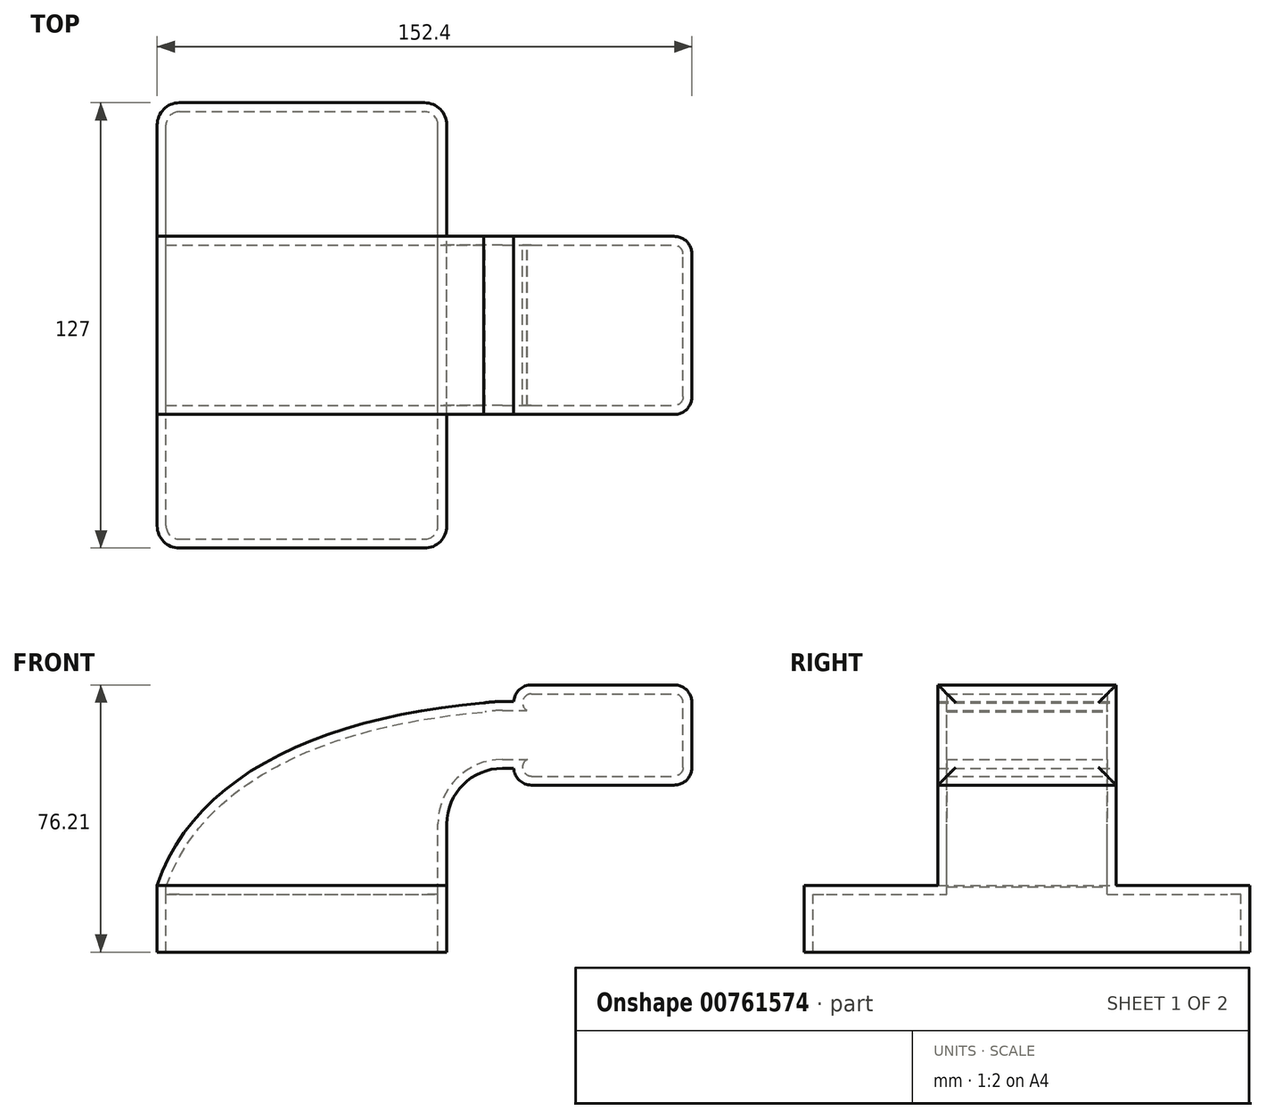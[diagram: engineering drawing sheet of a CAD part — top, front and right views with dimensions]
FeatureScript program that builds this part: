
annotation { "Feature Type Name" : "Feature", "Feature Type Description" : "" }
export const myFeature = defineFeature(function(context is Context, id is Id, definition is map)
    precondition{}
    {
        {
            var Q0;
            Q0=qCreatedBy(makeId("Front.planeOp"),FACE);
            var sketch = newSketch(context, id + "F0", { "sketchPlane" : qUnion([Q0])});
            skLineSegment(sketch, "E0.bottom", {"start": v(-41.28, -9.53) * mm, "end": v(41.28, -9.53) * mm});
            skLineSegment(sketch, "E0.top", {"start": v(-41.28, 9.52) * mm, "end": v(41.28, 9.52) * mm});
            skLineSegment(sketch, "E0.left", {"start": v(-41.28, -9.53) * mm, "end": v(-41.28, 9.53) * mm});
            skLineSegment(sketch, "E0.right", {"start": v(41.28, -9.53) * mm, "end": v(41.28, 9.52) * mm});
            skPoint(sketch, "E0.middle", {"position": v(0, 0) * mm});
            skLineSegment(sketch, "E1.bottom", {"start": v(60.33, 38.1) * mm, "end": v(111.13, 38.1) * mm});
            skLineSegment(sketch, "E1.top", {"start": v(60.33, 66.67) * mm, "end": v(111.13, 66.67) * mm});
            skLineSegment(sketch, "E1.left", {"start": v(60.33, 38.1) * mm, "end": v(60.33, 66.67) * mm});
            skLineSegment(sketch, "E1.right", {"start": v(111.13, 38.1) * mm, "end": v(111.13, 66.67) * mm});
            skPoint(sketch, "E1.middle", {"position": v(85.73, 52.39) * mm});
            skLineSegment(sketch, "E2", {"start": v(41.27, 9.52) * mm, "end": v(41.27, 27) * mm});
            skArc(sketch, "E3", {"start": v(41.27, 27) * mm, "mid": v(45.92, 38.23) * mm, "end": v(57.15, 42.88) * mm});
            skLineSegment(sketch, "E4", {"start": v(57.15, 42.88) * mm, "end": v(85.82, 42.88) * mm});
            skLineSegment(sketch, "E5.0", {"start": v(57.15, 61.93) * mm, "end": v(85.82, 61.93) * mm});
            skArc(sketch, "E5.1", {"start": v(22.23, 27) * mm, "mid": v(32.45, 51.7) * mm, "end": v(57.15, 61.93) * mm});
            skLineSegment(sketch, "E5.2", {"start": v(22.22, 9.52) * mm, "end": v(22.22, 27) * mm});
            skLineSegment(sketch, "E6", {"start": v(85.82, 38.1) * mm, "end": v(85.82, 66.67) * mm});
            skFitSpline(sketch, "E7", {"points": [v(-41.28, 9.53) * mm, v(57.15, 61.93) * mm], "startDerivative": vector(32.2, 96.48) * mm, "endDerivative": vector(149.38, 9.9) * mm});
            skSolve(sketch);
        }
        {
            var Q0;
            Q0=makeQuery(id+"F0.imprint","IMPRINT",FACE,{"disambiguationData":[TD([[makeQuery(id+"F0.imprint","IMPRINT",EDGE,{"derivedFrom":sQuery(id+"F0.wireOp",EDGE,"E0.bottom")}),1.0]])]});
            extrude(context, id + "F1", {"entities" : qUnion([Q0]), "endBound" : BoundingType.SYMMETRIC, "depth" : 127 * mm, "offsetDistance" : 25.4 * mm});
        }
        {
            var Q0;
            Q0 = qSketchRegion(id + "F0", true);
            extrude(context, id + "F2", {"entities" : qUnion([Q0]), "operationType" : NewBodyOperationType.ADD, "endBound" : BoundingType.SYMMETRIC, "depth" : 50.8 * mm, "offsetDistance" : 25.4 * mm});
        }
        {
            var Q0;
            Q0=makeQuery(id+"F1.opExtrude","CAP_EDGE",EDGE,{"disambiguationData":[OSD([sQuery(id+"F0.wireOp",EDGE,"E0.right")])],"isStart":false});
            var Q1;
            Q1=makeQuery(id+"F1.opExtrude","CAP_EDGE",EDGE,{"disambiguationData":[OSD([sQuery(id+"F0.wireOp",EDGE,"E0.left")])],"isStart":false});
            var Q2;
            Q2=makeQuery(id+"F1.opExtrude","CAP_EDGE",EDGE,{"disambiguationData":[OSD([sQuery(id+"F0.wireOp",EDGE,"E0.left")])],"isStart":true});
            var Q3;
            Q3=makeQuery(id+"F1.opExtrude","CAP_EDGE",EDGE,{"disambiguationData":[OSD([sQuery(id+"F0.wireOp",EDGE,"E0.right")])],"isStart":true});
            fillet(context, id + "F3", {"entities" : qUnion([Q0, Q1, Q2, Q3]), "radius" : 6.35 * mm, "tangentPropagation" : true, "allowEdgeOverflow" : false});
        }
        {
            var Q0;
            Q0=makeQuery(id+"F2.opExtrude","CAP_EDGE",EDGE,{"disambiguationData":[OSD([sQuery(id+"F0.wireOp",EDGE,"E1.right")])],"isStart":false});
            var Q1;
            Q1=makeQuery(id+"F2.opExtrude","CAP_EDGE",EDGE,{"disambiguationData":[OSD([sQuery(id+"F0.wireOp",EDGE,"E1.right")])],"isStart":true});
            var Q2;
            Q2=makeQuery(id+"F2.opExtrude","SWEPT_EDGE",EDGE,{"disambiguationData":[OSD([sQuery(id+"F0.wireOp",EDGE,"E1.bottom"),sQuery(id+"F0.wireOp",EDGE,"E1.right")])]});
            var Q3;
            Q3=makeQuery(id+"F2.opExtrude","SWEPT_EDGE",EDGE,{"disambiguationData":[OSD([sQuery(id+"F0.wireOp",EDGE,"E1.top"),sQuery(id+"F0.wireOp",EDGE,"E1.right")])]});
            fillet(context, id + "F4", {"entities" : qUnion([Q0, Q1, Q2, Q3]), "radius" : 5.08 * mm, "tangentPropagation" : true, "allowEdgeOverflow" : false});
        }
        {
            var Q0;
            Q0=makeQuery(id+"F2.opExtrude","SWEPT_EDGE",EDGE,{"disambiguationData":[OSD([sQuery(id+"F0.wireOp",EDGE,"E1.top"),sQuery(id+"F0.wireOp",EDGE,"E1.left")])]});
            var Q1;
            Q1=makeQuery(id+"F2.opExtrude","SWEPT_EDGE",EDGE,{"disambiguationData":[OSD([sQuery(id+"F0.wireOp",EDGE,"E3"),sQuery(id+"F0.wireOp",EDGE,"E4")])]});
            var Q2;
            Q2=makeQuery(id+"F2.opExtrude","SWEPT_EDGE",EDGE,{"disambiguationData":[OSD([sQuery(id+"F0.wireOp",EDGE,"E1.bottom"),sQuery(id+"F0.wireOp",EDGE,"E1.left")])]});
            fillet(context, id + "F5", {"entities" : qUnion([Q0, Q1, Q2]), "radius" : 5.08 * mm, "tangentPropagation" : true, "allowEdgeOverflow" : false});
        }
        {
            var Q0;
            Q0=makeQuery(id+"F1.opExtrude","SWEPT_FACE",FACE,{"disambiguationData":[OSD([sQuery(id+"F0.wireOp",EDGE,"E0.bottom")])]});
            shell(context, id + "F6", {"entities" : qUnion([Q0]), "thickness" : 2.54 * mm});
        }
    });
